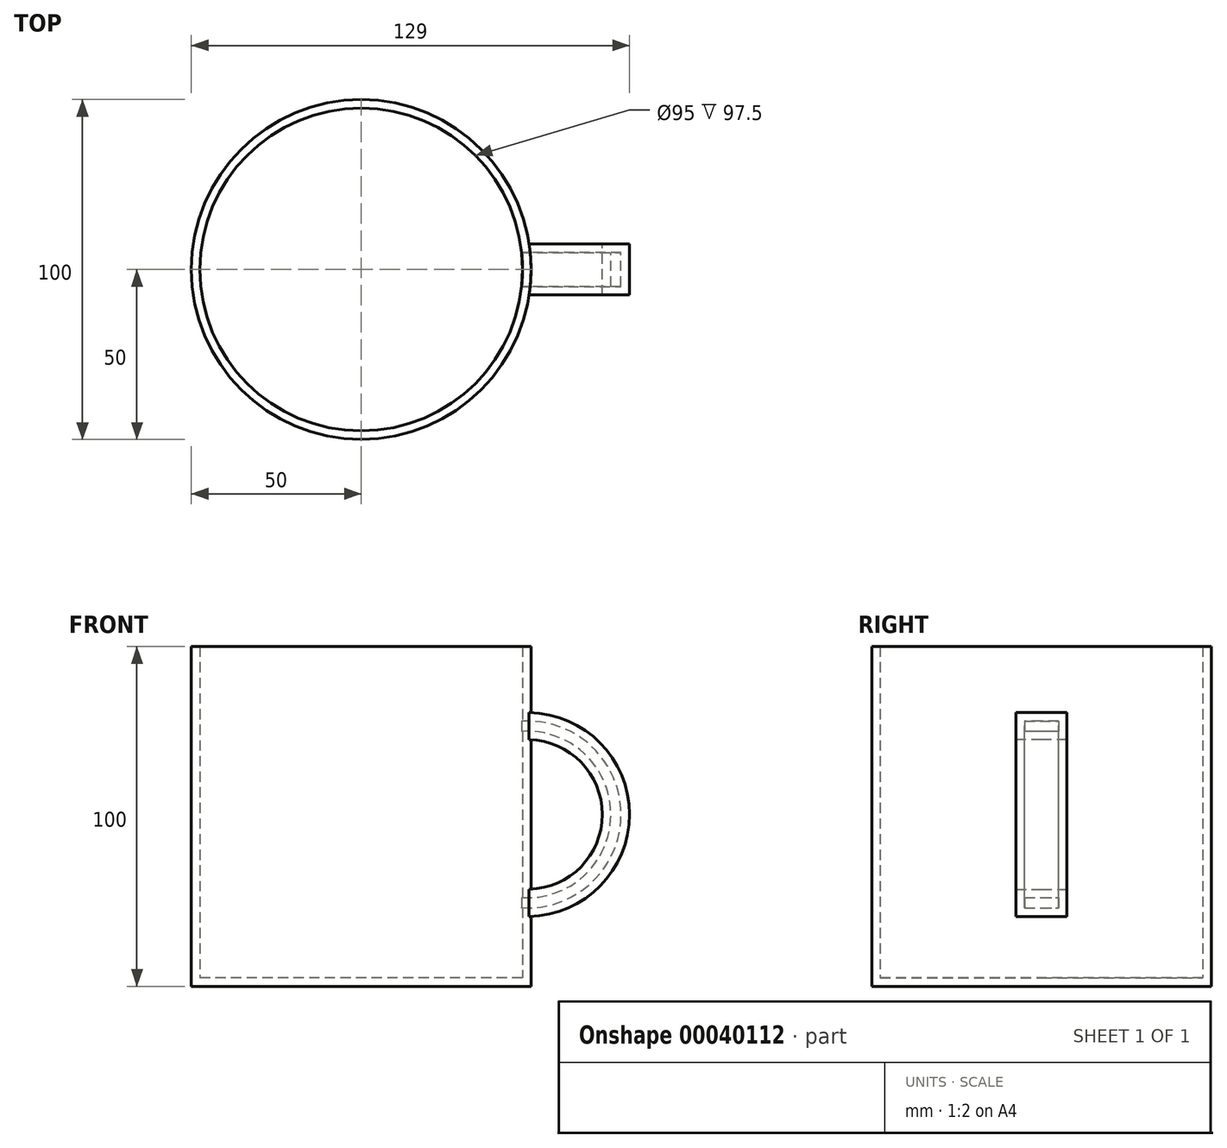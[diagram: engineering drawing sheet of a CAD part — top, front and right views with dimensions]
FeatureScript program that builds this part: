
annotation { "Feature Type Name" : "Feature", "Feature Type Description" : "" }
export const myFeature = defineFeature(function(context is Context, id is Id, definition is map)
    precondition{}
    {
        {
            var Q0;
            Q0=qCreatedBy(makeId("Top.planeOp"),FACE);
            var sketch = newSketch(context, id + "F0", { "sketchPlane" : qUnion([Q0])});
            skCircle(sketch, "E0", {"center": v(0, 0) * mm, "radius": 50 * mm});
            skSolve(sketch);
        }
        {
            var Q0;
            Q0=makeQuery(id+"F0.imprint","IMPRINT",FACE,{"disambiguationData":[TD([[makeQuery(id+"F0.imprint","IMPRINT",EDGE,{"derivedFrom":sQuery(id+"F0.wireOp",EDGE,"E0")}),1.0]])]});
            extrude(context, id + "F1", {"entities" : qUnion([Q0]), "depth" : 100 * mm});
        }
        {
            var Q0;
            Q0=qCreatedBy(makeId("Front.planeOp"),FACE);
            var sketch = newSketch(context, id + "F2", { "sketchPlane" : qUnion([Q0])});
            skArc(sketch, "E1", {"start": v(49, 20.57) * mm, "mid": v(79, 50.57) * mm, "end": v(49, 80.57) * mm});
            skArc(sketch, "E2.0", {"start": v(49, 28.57) * mm, "mid": v(71, 50.57) * mm, "end": v(49, 72.57) * mm});
            skLineSegment(sketch, "E3", {"start": v(49, 80.57) * mm, "end": v(49, 72.57) * mm});
            skLineSegment(sketch, "E4.trimOffspring", {"start": v(49, 28.57) * mm, "end": v(49, 20.57) * mm});
            skSolve(sketch);
        }
        {
            var Q0;
            Q0=makeQuery(id+"F2.imprint","IMPRINT",FACE,{"disambiguationData":[TD([[makeQuery(id+"F2.imprint","IMPRINT",EDGE,{"derivedFrom":sQuery(id+"F2.wireOp",EDGE,"E1")}),1.0]])]});
            extrude(context, id + "F3", {"entities" : qUnion([Q0]), "operationType" : NewBodyOperationType.ADD, "depth" : 7.5 * mm, "hasSecondDirection" : true, "secondDirectionOppositeDirection" : true, "secondDirectionDepth" : 7.5 * mm});
        }
        {
            var Q0;
            Q0=makeQuery(id+"F1.opExtrude","CAP_FACE",FACE,{"disambiguationData":[OSD([sQuery(id+"F0.wireOp",EDGE,"E0")])],"isStart":false});
            shell(context, id + "F4", {"entities" : qUnion([Q0]), "thickness" : 2.5 * mm});
        }
    });
